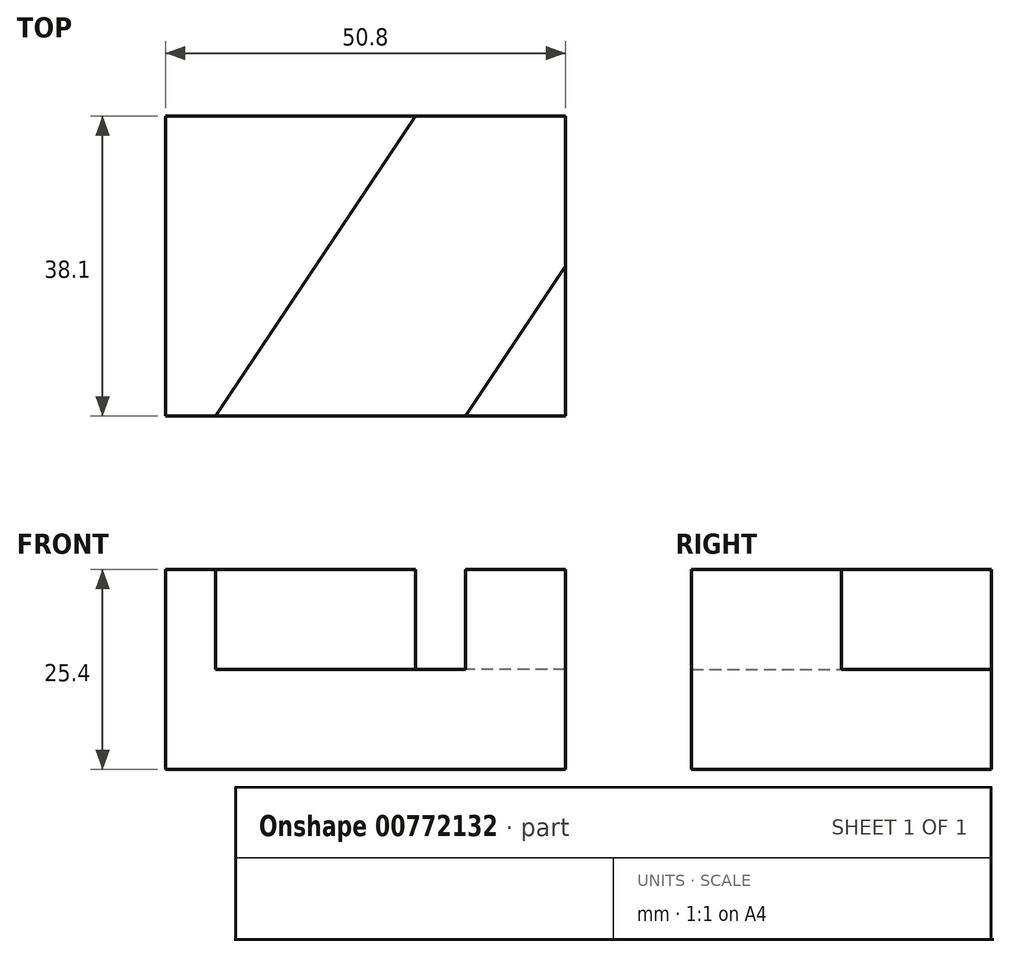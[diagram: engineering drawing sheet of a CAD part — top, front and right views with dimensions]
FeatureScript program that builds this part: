
annotation { "Feature Type Name" : "Feature", "Feature Type Description" : "" }
export const myFeature = defineFeature(function(context is Context, id is Id, definition is map)
    precondition{}
    {
        {
            var Q0;
            Q0=qCreatedBy(makeId("Front.planeOp"),FACE);
            var sketch = newSketch(context, id + "F0", { "sketchPlane" : qUnion([Q0])});
            skLineSegment(sketch, "E0", {"start": v(0, 0) * mm, "end": v(50.8, 0) * mm});
            skLineSegment(sketch, "E1", {"start": v(50.8, 0) * mm, "end": v(50.8, 25.4) * mm});
            skLineSegment(sketch, "E2", {"start": v(50.8, 25.4) * mm, "end": v(0, 25.4) * mm});
            skLineSegment(sketch, "E3", {"start": v(0, 25.4) * mm, "end": v(0, 0) * mm});
            skSolve(sketch);
        }
        {
            var Q0;
            Q0 = qSketchRegion(id + "F0", true);
            extrude(context, id + "F1", {"entities" : qUnion([Q0]), "depth" : 38.1 * mm, "offsetDistance" : 25.4 * mm});
        }
        {
            var Q0;
            Q0=makeQuery(id+"F1.opExtrude","SWEPT_FACE",FACE,{"disambiguationData":[OSD([sQuery(id+"F0.wireOp",EDGE,"E2")])]});
            var sketch = newSketch(context, id + "F2", { "sketchPlane" : qUnion([Q0])});
            skLineSegment(sketch, "E4", {"start": v(0, 0) * mm, "end": v(31.75, 0) * mm});
            skLineSegment(sketch, "E5", {"start": v(0, -38.1) * mm, "end": v(6.35, -38.1) * mm});
            skLineSegment(sketch, "E6", {"start": v(6.35, -38.1) * mm, "end": v(31.75, 0) * mm});
            skLineSegment(sketch, "E7", {"start": v(6.35, -38.1) * mm, "end": v(38.1, -38.1) * mm});
            skLineSegment(sketch, "E8", {"start": v(50.8, 0) * mm, "end": v(50.8, -19.05) * mm});
            skLineSegment(sketch, "E9", {"start": v(50.8, -19.05) * mm, "end": v(38.1, -38.1) * mm});
            skSolve(sketch);
        }
        {
            var Q0;
            Q0 = qSketchRegion(id + "F2", true);
            var Q1;
            {var subQ1=sQuery(id+"F2.wireOp",EDGE,"E6");Q1=makeQuery(id+"F2.imprint","IMPRINT",FACE,{"disambiguationData":[TD([[makeQuery(id+"F2.imprint","IMPRINT",EDGE,{"derivedFrom":subQ1}),-1.0]])]});}
            extrude(context, id + "F3", {"entities" : qUnion([Q0, Q1]), "operationType" : NewBodyOperationType.REMOVE, "oppositeDirection" : true, "depth" : 12.7 * mm, "offsetDistance" : 25.4 * mm});
        }
    });
